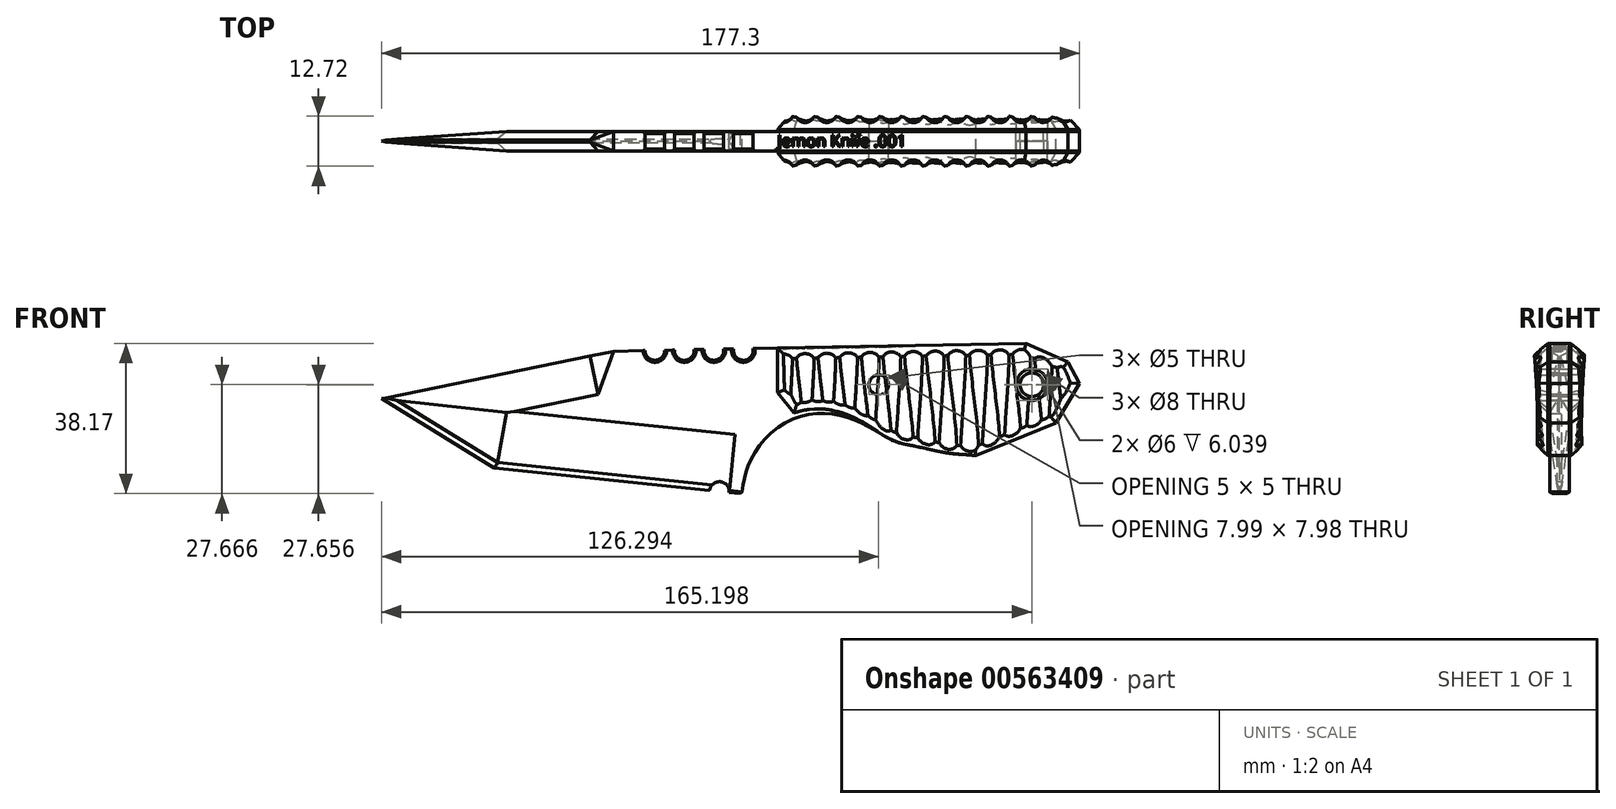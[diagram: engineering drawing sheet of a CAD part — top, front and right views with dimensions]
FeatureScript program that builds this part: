
annotation { "Feature Type Name" : "Feature", "Feature Type Description" : "" }
export const myFeature = defineFeature(function(context is Context, id is Id, definition is map)
    precondition{}
    {
        {
            var Q0;
            Q0=qCreatedBy(makeId("Front.planeOp"),FACE);
            var sketch = newSketch(context, id + "F0", { "sketchPlane" : qUnion([Q0])});
            skLineSegment(sketch, "E0", {"start": v(87.5, 0) * mm, "end": v(-87.5, 0) * mm, "construction": true});
            skLineSegment(sketch, "E1", {"start": v(-87.5, 0) * mm, "end": v(-28.6, 12.06) * mm});
            skLineSegment(sketch, "E2", {"start": v(-28.6, 12.06) * mm, "end": v(-20.58, 12.2) * mm});
            skLineSegment(sketch, "E3", {"start": v(76.15, 14.06) * mm, "end": v(86.87, 9.34) * mm});
            skLineSegment(sketch, "E4", {"start": v(86.87, 9.34) * mm, "end": v(89.8, 3.9) * mm});
            skLineSegment(sketch, "E5", {"start": v(89.8, 3.9) * mm, "end": v(83.87, -6.17) * mm});
            skLineSegment(sketch, "E6", {"start": v(83.87, -6.17) * mm, "end": v(63.5, -14.46) * mm});
            skLineSegment(sketch, "E7", {"start": v(-87.5, 0) * mm, "end": v(-58.95, -17.62) * mm});
            skLineSegment(sketch, "E8", {"start": v(-58.95, -17.62) * mm, "end": v(-4.16, -23.31) * mm});
            skFitSpline(sketch, "E9", {"points": [v(3.95, -24.15) * mm, v(5.88, -16.34) * mm, v(13.42, -7.16) * mm, v(24.63, -3.72) * mm, v(34.48, -6.24) * mm, v(42.3, -10.21) * mm, v(48.07, -12.01) * mm, v(55.88, -13.58) * mm, v(63.5, -14.46) * mm], "startDerivative": vector(14.8, 75.55) * mm, "endDerivative": vector(64.9, -6.2) * mm});
            skCircle(sketch, "E10", {"center": v(38.8, 3.56) * mm, "radius": 2.5 * mm});
            skCircle(sketch, "E11", {"center": v(77.7, 3.56) * mm, "radius": 4 * mm});
            skArc(sketch, "E12", {"start": v(-20.58, 12.2) * mm, "mid": v(-18.03, 9.76) * mm, "end": v(-15.58, 12.3) * mm});
            skArc(sketch, "E13.1.0.0", {"start": v(-13.08, 12.35) * mm, "mid": v(-10.53, 9.76) * mm, "end": v(-8.09, 12.45) * mm});
            skArc(sketch, "E13.2.0.0", {"start": v(-5.57, 12.5) * mm, "mid": v(-3.03, 9.76) * mm, "end": v(-0.6, 12.6) * mm});
            skArc(sketch, "E13.3.0.0", {"start": v(1.95, 12.64) * mm, "mid": v(4.47, 9.76) * mm, "end": v(6.87, 12.73) * mm});
            skLineSegment(sketch, "E13.direction1", {"start": v(-18.08, 12.26) * mm, "end": v(-10.58, 12.26) * mm, "construction": true});
            skLineSegment(sketch, "E14.trimOffspring", {"start": v(6.87, 12.73) * mm, "end": v(76.15, 14.06) * mm});
            skLineSegment(sketch, "E15.trimOffspring", {"start": v(-0.6, 12.6) * mm, "end": v(1.95, 12.64) * mm});
            skLineSegment(sketch, "E16.trimOffspring", {"start": v(-8.09, 12.45) * mm, "end": v(-5.57, 12.5) * mm});
            skLineSegment(sketch, "E17.trimOffspring", {"start": v(-15.58, 12.3) * mm, "end": v(-13.08, 12.35) * mm});
            skArc(sketch, "E18", {"start": v(0.82, -23.83) * mm, "mid": v(-1.41, -21.08) * mm, "end": v(-4.16, -23.31) * mm});
            skLineSegment(sketch, "E19.trimOffspring", {"start": v(0.82, -23.83) * mm, "end": v(3.95, -24.15) * mm});
            skSolve(sketch);
        }
        {
            var Q0;
            Q0 = qSketchRegion(id + "F0", true);
            extrude(context, id + "F1", {"entities" : qUnion([Q0]), "depth" : 5 * mm, "offsetDistance" : 25 * mm, "symmetric" : true});
        }
        {
            var Q0;
            Q0=makeQuery(id+"F1.opExtrude","SWEPT_FACE",FACE,{"disambiguationData":[OSD([sQuery(id+"F0.wireOp",EDGE,"E19.trimOffspring")])]});
            var Q1;
            Q1=makeQuery(id+"F1.opExtrude","SWEPT_EDGE",EDGE,{"disambiguationData":[OSD([sQuery(id+"F0.wireOp",EDGE,"E18"),sQuery(id+"F0.wireOp",EDGE,"E19.trimOffspring")])]});
            cPlane(context, id + "F2", {"entities" : qUnion([Q0, Q1]), "cplaneType" : CPlaneType.LINE_ANGLE, "offset" : 25 * mm, "angle" : 90 * degree, "width" : 150 * mm, "height" : 150 * mm});
        }
        {
            var Q0;
            Q0=qCreatedBy(id+"F2.planeOp",FACE);
            var sketch = newSketch(context, id + "F3", { "sketchPlane" : qUnion([Q0])});
            skLineSegment(sketch, "E20", {"start": v(0, -23.94) * mm, "end": v(0, -10.63) * mm, "construction": true});
            skLineSegment(sketch, "E21", {"start": v(-2.53, -8.62) * mm, "end": v(-2.53, -24.28) * mm});
            skLineSegment(sketch, "E22", {"start": v(-2.53, -24.28) * mm, "end": v(0, -24.28) * mm});
            skLineSegment(sketch, "E23", {"start": v(0, -23.94) * mm, "end": v(-0.25, -23.94) * mm});
            skLineSegment(sketch, "E24", {"start": v(-0.25, -23.94) * mm, "end": v(-2.53, -8.62) * mm});
            skLineSegment(sketch, "E25.MirrorCS", {"start": v(0.25, -23.94) * mm, "end": v(2.53, -8.62) * mm});
            skLineSegment(sketch, "E26.MirrorCS", {"start": v(0, -23.94) * mm, "end": v(0.25, -23.94) * mm});
            skLineSegment(sketch, "E27.MirrorCS", {"start": v(2.53, -24.28) * mm, "end": v(0, -24.28) * mm});
            skLineSegment(sketch, "E28.MirrorCS", {"start": v(2.53, -8.62) * mm, "end": v(2.53, -24.28) * mm});
            skSolve(sketch);
        }
        {
            var Q0;
            Q0 = qSketchRegion(id + "F3", true);
            extrude(context, id + "F4", {"entities" : qUnion([Q0]), "operationType" : NewBodyOperationType.REMOVE, "endBound" : BoundingType.THROUGH_ALL, "oppositeDirection" : true, "depth" : 25 * mm, "offsetDistance" : 25 * mm});
        }
        {
            var Q0;
            Q0=makeQuery(id+"F1.opExtrude","SWEPT_FACE",FACE,{"disambiguationData":[OSD([sQuery(id+"F0.wireOp",EDGE,"E7")])]});
            var Q1;
            Q1=makeQuery(id+"F1.opExtrude","SWEPT_EDGE",EDGE,{"disambiguationData":[OSD([sQuery(id+"F0.wireOp",EDGE,"E1"),sQuery(id+"F0.wireOp",EDGE,"E7")])]});
            cPlane(context, id + "F5", {"entities" : qUnion([Q0, Q1]), "cplaneType" : CPlaneType.LINE_ANGLE, "offset" : 25 * mm, "angle" : 90 * degree, "width" : 150 * mm, "height" : 150 * mm});
        }
        {
            var Q0;
            Q0=makeQuery(id+"F1.opExtrude","SWEPT_FACE",FACE,{"disambiguationData":[OSD([sQuery(id+"F0.wireOp",EDGE,"E1")])]});
            var Q1;
            Q1=makeQuery(id+"F1.opExtrude","SWEPT_EDGE",EDGE,{"disambiguationData":[OSD([sQuery(id+"F0.wireOp",EDGE,"E1"),sQuery(id+"F0.wireOp",EDGE,"E7")])]});
            cPlane(context, id + "F6", {"entities" : qUnion([Q0, Q1]), "cplaneType" : CPlaneType.LINE_ANGLE, "offset" : 25 * mm, "angle" : 90 * degree, "width" : 150 * mm, "height" : 150 * mm});
        }
        {
            var Q0;
            Q0=qCreatedBy(id+"F5.planeOp",FACE);
            var sketch = newSketch(context, id + "F7", { "sketchPlane" : qUnion([Q0])});
            skLineSegment(sketch, "E29", {"start": v(0, -45.96) * mm, "end": v(0, -23.67) * mm, "construction": true});
            skLineSegment(sketch, "E30", {"start": v(0, -45.96) * mm, "end": v(0.25, -45.96) * mm});
            skLineSegment(sketch, "E31", {"start": v(0.25, -45.96) * mm, "end": v(2.5, -31.86) * mm});
            skLineSegment(sketch, "E32", {"start": v(2.5, -31.86) * mm, "end": v(2.5, -46.86) * mm});
            skLineSegment(sketch, "E33", {"start": v(2.5, -46.86) * mm, "end": v(0, -46.86) * mm});
            skLineSegment(sketch, "E34.MirrorCS", {"start": v(-0.25, -45.96) * mm, "end": v(-2.5, -31.86) * mm});
            skLineSegment(sketch, "E35.MirrorCS", {"start": v(-2.5, -31.86) * mm, "end": v(-2.5, -46.86) * mm});
            skLineSegment(sketch, "E36.MirrorCS", {"start": v(-2.5, -46.86) * mm, "end": v(0, -46.86) * mm});
            skLineSegment(sketch, "E37.MirrorCS", {"start": v(0, -45.96) * mm, "end": v(-0.25, -45.96) * mm});
            skSolve(sketch);
        }
        {
            var Q0;
            Q0 = qSketchRegion(id + "F7", true);
            extrude(context, id + "F8", {"entities" : qUnion([Q0]), "operationType" : NewBodyOperationType.REMOVE, "endBound" : BoundingType.THROUGH_ALL, "depth" : 25 * mm, "offsetDistance" : 25 * mm});
        }
        {
            var Q0;
            Q0=qCreatedBy(id+"F6.planeOp",FACE);
            var sketch = newSketch(context, id + "F9", { "sketchPlane" : qUnion([Q0])});
            skFitSpline(sketch, "E38.0", {"points": [v(0.25, 17.54) * mm, v(0.08, 17.54) * mm, v(-0.08, 17.54) * mm, v(-0.25, 17.54) * mm], "construction": true});
            skFitSpline(sketch, "E39.0", {"points": [v(2.5, 17.54) * mm, v(2.5, 14.4) * mm, v(2.5, 11.26) * mm, v(2.5, 8.12) * mm], "construction": true});
            skLineSegment(sketch, "E40", {"start": v(0, 17.54) * mm, "end": v(0, 7.44) * mm, "construction": true});
            skLineSegment(sketch, "E41", {"start": v(2.5, 17.54) * mm, "end": v(2.5, 7.54) * mm});
            skLineSegment(sketch, "E42", {"start": v(2.5, 7.54) * mm, "end": v(0.25, 17.54) * mm});
            skLineSegment(sketch, "E43", {"start": v(2.5, 17.54) * mm, "end": v(2.5, 18.15) * mm});
            skLineSegment(sketch, "E44", {"start": v(2.5, 18.15) * mm, "end": v(0, 18.15) * mm});
            skLineSegment(sketch, "E45.MirrorCS", {"start": v(-2.5, 18.15) * mm, "end": v(0, 18.15) * mm});
            skLineSegment(sketch, "E46.MirrorCS", {"start": v(-2.5, 7.54) * mm, "end": v(-0.25, 17.54) * mm});
            skLineSegment(sketch, "E47.MirrorCS", {"start": v(-2.5, 17.54) * mm, "end": v(-2.5, 18.15) * mm});
            skFitSpline(sketch, "E48.MirrorCS", {"points": [v(-2.5, 17.54) * mm, v(-2.5, 14.4) * mm, v(-2.5, 11.26) * mm, v(-2.5, 8.12) * mm], "construction": true});
            skLineSegment(sketch, "E49.MirrorCS", {"start": v(-2.5, 17.54) * mm, "end": v(-2.5, 7.54) * mm});
            skLineSegment(sketch, "E50", {"start": v(-0.25, 17.54) * mm, "end": v(0.25, 17.54) * mm});
            skSolve(sketch);
        }
        {
            var Q0;
            Q0 = qSketchRegion(id + "F9", true);
            var Q1;
            Q1=makeQuery(id+"F1.opExtrude","CAP_VERTEX",VERTEX,{"disambiguationData":[OSD([sQuery(id+"F0.wireOp",EDGE,"E1"),sQuery(id+"F0.wireOp",EDGE,"E2")])],"isStart":false});
            extrude(context, id + "F10", {"entities" : qUnion([Q0]), "operationType" : NewBodyOperationType.REMOVE, "endBound" : BoundingType.UP_TO_VERTEX, "oppositeDirection" : true, "depth" : 57.81 * mm, "endBoundEntityVertex" : qUnion([Q1]), "offsetDistance" : 25 * mm});
        }
        {
            var Q0;
            Q0=makeQuery(id+"F10.boolean.opBoolean","COPY",EDGE,{"derivedFrom":makeQuery(id+"F10.opExtrude","CAP_EDGE",EDGE,{"disambiguationData":[OSD([sQuery(id+"F9.wireOp",EDGE,"E42")])],"isStart":false})});
            chamfer(context, id + "F11", {"entities" : qUnion([Q0]), "chamferType" : ChamferType.OFFSET_ANGLE, "width" : 2.19 * mm, "oppositeDirection" : true, "angle" : 70 * degree, "tangentPropagation" : true});
        }
        {
            var Q0;
            Q0=makeQuery(id+"F10.boolean.opBoolean","COPY",EDGE,{"derivedFrom":makeQuery(id+"F10.opExtrude","CAP_EDGE",EDGE,{"disambiguationData":[OSD([sQuery(id+"F9.wireOp",EDGE,"E46.MirrorCS")])],"isStart":false})});
            chamfer(context, id + "F12", {"entities" : qUnion([Q0]), "chamferType" : ChamferType.OFFSET_ANGLE, "width" : 2.19 * mm, "oppositeDirection" : false, "angle" : 70 * degree, "tangentPropagation" : true});
        }
        {
            var Q0;
            Q0=makeQuery(id+"F1.opExtrude","CAP_FACE",FACE,{"disambiguationData":[OSD([sQuery(id+"F0.wireOp",EDGE,"E1"),sQuery(id+"F0.wireOp",EDGE,"E2"),sQuery(id+"F0.wireOp",EDGE,"E3"),sQuery(id+"F0.wireOp",EDGE,"E4"),sQuery(id+"F0.wireOp",EDGE,"E5"),sQuery(id+"F0.wireOp",EDGE,"E6"),sQuery(id+"F0.wireOp",EDGE,"E7"),sQuery(id+"F0.wireOp",EDGE,"E8"),sQuery(id+"F0.wireOp",EDGE,"E9"),sQuery(id+"F0.wireOp",EDGE,"E10"),sQuery(id+"F0.wireOp",EDGE,"E11"),sQuery(id+"F0.wireOp",EDGE,"E12"),sQuery(id+"F0.wireOp",EDGE,"E13.1.0.0"),sQuery(id+"F0.wireOp",EDGE,"E13.2.0.0"),sQuery(id+"F0.wireOp",EDGE,"E13.3.0.0"),sQuery(id+"F0.wireOp",EDGE,"E14.trimOffspring"),sQuery(id+"F0.wireOp",EDGE,"E15.trimOffspring"),sQuery(id+"F0.wireOp",EDGE,"E16.trimOffspring"),sQuery(id+"F0.wireOp",EDGE,"E17.trimOffspring"),sQuery(id+"F0.wireOp",EDGE,"E18"),sQuery(id+"F0.wireOp",EDGE,"E19.trimOffspring")])],"isStart":false});
            var sketch = newSketch(context, id + "F13", { "sketchPlane" : qUnion([Q0])});
            skLineSegment(sketch, "E51.0", {"start": v(13.04, 12.85) * mm, "end": v(76.15, 14.06) * mm});
            skLineSegment(sketch, "E52.0", {"start": v(76.15, 14.06) * mm, "end": v(86.87, 9.34) * mm});
            skLineSegment(sketch, "E53.0", {"start": v(86.87, 9.34) * mm, "end": v(89.8, 3.9) * mm});
            skLineSegment(sketch, "E54.0", {"start": v(89.8, 3.9) * mm, "end": v(83.87, -6.17) * mm});
            skLineSegment(sketch, "E55.0", {"start": v(83.87, -6.17) * mm, "end": v(63.5, -14.46) * mm});
            skFitSpline(sketch, "E56.0", {"points": [v(3.95, -24.15) * mm, v(4.54, -21.17) * mm, v(5, -16.2) * mm, v(12.74, -5.92) * mm, v(24.62, -2.63) * mm, v(34.48, -5.81) * mm, v(42.13, -10.52) * mm, v(48.02, -12.06) * mm, v(55.94, -13.74) * mm, v(61, -14.22) * mm, v(63.5, -14.46) * mm]});
            skLineSegment(sketch, "E57", {"start": v(13.04, 12.85) * mm, "end": v(13.04, 1.61) * mm});
            skLineSegment(sketch, "E58", {"start": v(13.04, 1.61) * mm, "end": v(18.26, -4.73) * mm});
            skCircle(sketch, "E59.0", {"center": v(38.8, 3.56) * mm, "radius": 2.5 * mm});
            skCircle(sketch, "E60.0", {"center": v(77.7, 3.56) * mm, "radius": 4 * mm});
            skSolve(sketch);
        }
        {
            var Q0;
            Q0 = qSketchRegion(id + "F13", true);
            extrude(context, id + "F14", {"entities" : qUnion([Q0]), "depth" : 4 * mm, "offsetDistance" : 25 * mm});
        }
        {
            var Q0;
            Q0=makeQuery(id+"F14.opExtrude","CAP_EDGE",EDGE,{"disambiguationData":[OSD([sQuery(id+"F13.wireOp",EDGE,"E57")])],"isStart":false});
            var Q1;
            Q1=makeQuery(id+"F14.opExtrude","CAP_EDGE",EDGE,{"disambiguationData":[OSD([sQuery(id+"F13.wireOp",EDGE,"E51.0")])],"isStart":false});
            var Q2;
            Q2=makeQuery(id+"F14.opExtrude","CAP_EDGE",EDGE,{"disambiguationData":[OSD([sQuery(id+"F13.wireOp",EDGE,"E52.0")])],"isStart":false});
            var Q3;
            Q3=makeQuery(id+"F14.opExtrude","CAP_EDGE",EDGE,{"disambiguationData":[OSD([sQuery(id+"F13.wireOp",EDGE,"E53.0")])],"isStart":false});
            var Q4;
            Q4=makeQuery(id+"F14.opExtrude","CAP_EDGE",EDGE,{"disambiguationData":[OSD([sQuery(id+"F13.wireOp",EDGE,"E54.0")])],"isStart":false});
            var Q5;
            Q5=makeQuery(id+"F14.opExtrude","CAP_EDGE",EDGE,{"disambiguationData":[OSD([sQuery(id+"F13.wireOp",EDGE,"E55.0")])],"isStart":false});
            var Q6;
            Q6=makeQuery(id+"F14.opExtrude","CAP_EDGE",EDGE,{"disambiguationData":[OSD([sQuery(id+"F13.wireOp",EDGE,"E56.0")])],"isStart":false});
            var Q7;
            Q7=makeQuery(id+"F14.opExtrude","CAP_EDGE",EDGE,{"disambiguationData":[OSD([sQuery(id+"F13.wireOp",EDGE,"E58")])],"isStart":false});
            chamfer(context, id + "F15", {"entities" : qUnion([Q0, Q1, Q2, Q3, Q4, Q5, Q6, Q7]), "chamferType" : ChamferType.OFFSET_ANGLE, "width" : 3 * mm, "oppositeDirection" : false, "angle" : 50 * degree, "tangentPropagation" : true});
        }
        {
            var Q0;
            Q0=qCreatedBy(id+"F2.planeOp",FACE);
            var sketch = newSketch(context, id + "F16", { "sketchPlane" : qUnion([Q0])});
            skLineSegment(sketch, "E61.0", {"start": v(-0.3, -23.62) * mm, "end": v(0.3, -23.62) * mm, "construction": true});
            skLineSegment(sketch, "E62", {"start": v(0, -23.62) * mm, "end": v(0, -22.12) * mm, "construction": true});
            skPoint(sketch, "E62.startSnap0", {"position": v(0, -23.62) * mm});
            skLineSegment(sketch, "E63", {"start": v(-0.53, -22.12) * mm, "end": v(-0.5, -23.75) * mm});
            skLineSegment(sketch, "E64", {"start": v(-0.5, -23.75) * mm, "end": v(0, -23.74) * mm});
            skLineSegment(sketch, "E65", {"start": v(-0.53, -22.12) * mm, "end": v(0, -23.62) * mm});
            skLineSegment(sketch, "E66.MirrorCS", {"start": v(0.53, -22.12) * mm, "end": v(0, -23.62) * mm});
            skLineSegment(sketch, "E67.MirrorCS", {"start": v(0.53, -22.12) * mm, "end": v(0.5, -23.75) * mm});
            skLineSegment(sketch, "E68.MirrorCS", {"start": v(0.5, -23.75) * mm, "end": v(0, -23.74) * mm});
            skSolve(sketch);
        }
        {
            var Q0;
            Q0 = qSketchRegion(id + "F16", true);
            extrude(context, id + "F17", {"entities" : qUnion([Q0]), "operationType" : NewBodyOperationType.REMOVE, "endBound" : BoundingType.THROUGH_ALL, "oppositeDirection" : true, "depth" : 25 * mm, "offsetDistance" : 25 * mm});
        }
        {
            var Q0;
            Q0=qCreatedBy(id+"F5.planeOp",FACE);
            var sketch = newSketch(context, id + "F18", { "sketchPlane" : qUnion([Q0])});
            skFitSpline(sketch, "E69.0", {"points": [v(-0.25, -45.96) * mm, v(-0.08, -45.96) * mm, v(0.08, -45.96) * mm, v(0.25, -45.96) * mm], "construction": true});
            skLineSegment(sketch, "E70", {"start": v(0, -45.96) * mm, "end": v(0, -44.2) * mm, "construction": true});
            skLineSegment(sketch, "E71", {"start": v(0.54, -44.2) * mm, "end": v(0.54, -46.08) * mm});
            skLineSegment(sketch, "E72", {"start": v(0.54, -46.08) * mm, "end": v(0, -46.08) * mm});
            skPoint(sketch, "E73.orphan", {"position": v(2.45, -32.2) * mm});
            skPoint(sketch, "E74.0.start.orphan", {"position": v(0.25, -45.96) * mm});
            skLineSegment(sketch, "E75", {"start": v(0, -45.96) * mm, "end": v(0.54, -44.2) * mm});
            skLineSegment(sketch, "E76.MirrorCS", {"start": v(0, -45.96) * mm, "end": v(-0.54, -44.2) * mm});
            skLineSegment(sketch, "E77.MirrorCS", {"start": v(-0.54, -44.2) * mm, "end": v(-0.54, -46.08) * mm});
            skLineSegment(sketch, "E78.MirrorCS", {"start": v(-0.54, -46.08) * mm, "end": v(0, -46.08) * mm});
            skSolve(sketch);
        }
        {
            var Q0;
            Q0 = qSketchRegion(id + "F18", true);
            extrude(context, id + "F19", {"entities" : qUnion([Q0]), "operationType" : NewBodyOperationType.REMOVE, "endBound" : BoundingType.THROUGH_ALL, "depth" : 25 * mm, "offsetDistance" : 25 * mm});
        }
        {
            var Q0;
            Q0=makeQuery(id+"F14.opExtrude","CAP_FACE",FACE,{"disambiguationData":[OSD([sQuery(id+"F13.wireOp",EDGE,"E51.0"),sQuery(id+"F13.wireOp",EDGE,"E52.0"),sQuery(id+"F13.wireOp",EDGE,"E53.0"),sQuery(id+"F13.wireOp",EDGE,"E54.0"),sQuery(id+"F13.wireOp",EDGE,"E55.0"),sQuery(id+"F13.wireOp",EDGE,"E56.0"),sQuery(id+"F13.wireOp",EDGE,"E57"),sQuery(id+"F13.wireOp",EDGE,"E58"),sQuery(id+"F13.wireOp",EDGE,"E59.0"),sQuery(id+"F13.wireOp",EDGE,"E60.0")])],"isStart":false});
            var sketch = newSketch(context, id + "F20", { "sketchPlane" : qUnion([Q0])});
            skCircle(sketch, "E79.0", {"center": v(38.8, 3.56) * mm, "radius": 2.5 * mm});
            skSolve(sketch);
        }
        {
            var Q0;
            Q0 = qSketchRegion(id + "F20", true);
            extrude(context, id + "F21", {"entities" : qUnion([Q0]), "oppositeDirection" : true, "depth" : 6.5 * mm, "offsetDistance" : 25 * mm});
        }
        {
            var Q0;
            Q0=makeQuery(id+"F14.opExtrude","CAP_FACE",FACE,{"disambiguationData":[OSD([sQuery(id+"F13.wireOp",EDGE,"E51.0"),sQuery(id+"F13.wireOp",EDGE,"E52.0"),sQuery(id+"F13.wireOp",EDGE,"E53.0"),sQuery(id+"F13.wireOp",EDGE,"E54.0"),sQuery(id+"F13.wireOp",EDGE,"E55.0"),sQuery(id+"F13.wireOp",EDGE,"E56.0"),sQuery(id+"F13.wireOp",EDGE,"E57"),sQuery(id+"F13.wireOp",EDGE,"E58"),sQuery(id+"F13.wireOp",EDGE,"E59.0"),sQuery(id+"F13.wireOp",EDGE,"E60.0")])],"isStart":false});
            var sketch = newSketch(context, id + "F22", { "sketchPlane" : qUnion([Q0])});
            skCircle(sketch, "E80.0", {"center": v(77.7, 3.56) * mm, "radius": 4 * mm});
            skCircle(sketch, "E81", {"center": v(77.7, 3.56) * mm, "radius": 3 * mm});
            skSolve(sketch);
        }
        {
            var Q0;
            Q0 = qSketchRegion(id + "F22", true);
            extrude(context, id + "F23", {"entities" : qUnion([Q0]), "oppositeDirection" : true, "depth" : 6.5 * mm, "offsetDistance" : 25 * mm});
        }
        {
            var Q0;
            Q0=makeQuery(id+"F1.opExtrude","SWEPT_FACE",FACE,{"disambiguationData":[OSD([sQuery(id+"F0.wireOp",EDGE,"E14.trimOffspring")])]});
            var Q1;
            Q1=makeQuery(id+"F14.opExtrude","CAP_EDGE",EDGE,{"disambiguationData":[OSD([sQuery(id+"F13.wireOp",EDGE,"E51.0")])],"isStart":true});
            cPlane(context, id + "F24", {"entities" : qUnion([Q0, Q1]), "cplaneType" : CPlaneType.LINE_ANGLE, "offset" : 25 * mm, "angle" : 178 * degree, "width" : 150 * mm, "height" : 150 * mm});
        }
        {
            var Q0;
            Q0=qCreatedBy(id+"F24.planeOp",FACE);
            var sketch = newSketch(context, id + "F25", { "sketchPlane" : qUnion([Q0])});
            skLineSegment(sketch, "E82", {"start": v(14.78, -7.64) * mm, "end": v(83.87, -7.64) * mm, "construction": true});
            skCircle(sketch, "E83", {"center": v(14.78, -7.64) * mm, "radius": 2.5 * mm});
            skCircle(sketch, "E84.1.0.0", {"center": v(20.28, -7.64) * mm, "radius": 2.5 * mm});
            skCircle(sketch, "E84.2.0.0", {"center": v(25.78, -7.64) * mm, "radius": 2.5 * mm});
            skCircle(sketch, "E84.3.0.0", {"center": v(31.28, -7.64) * mm, "radius": 2.5 * mm});
            skCircle(sketch, "E84.4.0.0", {"center": v(36.78, -7.64) * mm, "radius": 2.5 * mm});
            skCircle(sketch, "E84.5.0.0", {"center": v(42.28, -7.64) * mm, "radius": 2.5 * mm});
            skCircle(sketch, "E84.6.0.0", {"center": v(47.78, -7.64) * mm, "radius": 2.5 * mm});
            skCircle(sketch, "E84.7.0.0", {"center": v(53.28, -7.64) * mm, "radius": 2.5 * mm});
            skCircle(sketch, "E84.8.0.0", {"center": v(58.78, -7.64) * mm, "radius": 2.5 * mm});
            skCircle(sketch, "E84.9.0.0", {"center": v(64.28, -7.64) * mm, "radius": 2.5 * mm});
            skCircle(sketch, "E84.10.0.0", {"center": v(69.78, -7.64) * mm, "radius": 2.5 * mm});
            skCircle(sketch, "E84.11.0.0", {"center": v(75.28, -7.64) * mm, "radius": 2.5 * mm});
            skLineSegment(sketch, "E84.direction1", {"start": v(14.78, -7.64) * mm, "end": v(20.28, -7.64) * mm, "construction": true});
            skCircle(sketch, "E85.0.12.0", {"center": v(80.78, -7.64) * mm, "radius": 2.5 * mm});
            skCircle(sketch, "E85.0.13.0", {"center": v(86.28, -7.64) * mm, "radius": 2.5 * mm});
            skSolve(sketch);
        }
        {
            var Q0;
            Q0 = qSketchRegion(id + "F25", true);
            var Q1;
            Q1=sQuery(id+"F25.wireOp",EDGE,"E82");
            extrude(context, id + "F26", {"entities" : qUnion([Q0]), "operationType" : NewBodyOperationType.REMOVE, "surfaceEntities" : qUnion([Q1]), "endBound" : BoundingType.THROUGH_ALL, "oppositeDirection" : true, "depth" : 25 * mm, "offsetDistance" : 25 * mm});
        }
        {
            var Q0;
            Q0=qCreatedBy(makeId("Top.planeOp"),FACE);
            cPlane(context, id + "F27", {"entities" : qUnion([Q0]), "cplaneType" : CPlaneType.OFFSET, "offset" : 15 * mm, "oppositeDirection" : true, "width" : 150 * mm, "height" : 150 * mm});
        }
        {
            var Q0;
            Q0=qCreatedBy(id+"F27.planeOp",FACE);
            var sketch = newSketch(context, id + "F28", { "sketchPlane" : qUnion([Q0])});
            skLineSegment(sketch, "E86.0", {"start": v(89.8, -2.5) * mm, "end": v(89.8, 2.5) * mm, "construction": true});
            skLineSegment(sketch, "E87", {"start": v(118.57, 0) * mm, "end": v(61.03, 0) * mm, "construction": true});
            skPoint(sketch, "E87.startSnap0", {"position": v(89.8, 0) * mm});
            skPoint(sketch, "E87.endSnap0", {"position": v(89.8, 0) * mm});
            skSolve(sketch);
        }
        {
            var Q0;
            Q0=qCreatedBy(id+"F27.planeOp",FACE);
            var Q1;
            Q1=sQuery(id+"F28.wireOp",EDGE,"E87");
            cPlane(context, id + "F29", {"entities" : qUnion([Q0, Q1]), "cplaneType" : CPlaneType.LINE_ANGLE, "offset" : 25 * mm, "angle" : 175 * degree, "width" : 150 * mm, "height" : 150 * mm});
        }
        {
            var Q0;
            Q0=qCreatedBy(id+"F29.planeOp",FACE);
            var sketch = newSketch(context, id + "F30", { "sketchPlane" : qUnion([Q0])});
            skCircle(sketch, "E88", {"center": v(17.9, -7.67) * mm, "radius": 2.5 * mm});
            skCircle(sketch, "E89.1.0.0", {"center": v(23.4, -7.67) * mm, "radius": 2.5 * mm});
            skCircle(sketch, "E89.2.0.0", {"center": v(28.9, -7.67) * mm, "radius": 2.5 * mm});
            skCircle(sketch, "E89.3.0.0", {"center": v(34.4, -7.67) * mm, "radius": 2.5 * mm});
            skCircle(sketch, "E89.4.0.0", {"center": v(39.9, -7.67) * mm, "radius": 2.5 * mm});
            skCircle(sketch, "E89.5.0.0", {"center": v(45.4, -7.67) * mm, "radius": 2.5 * mm});
            skCircle(sketch, "E89.6.0.0", {"center": v(50.9, -7.67) * mm, "radius": 2.5 * mm});
            skCircle(sketch, "E89.7.0.0", {"center": v(56.4, -7.67) * mm, "radius": 2.5 * mm});
            skCircle(sketch, "E89.8.0.0", {"center": v(61.9, -7.67) * mm, "radius": 2.5 * mm});
            skCircle(sketch, "E89.9.0.0", {"center": v(67.4, -7.67) * mm, "radius": 2.5 * mm});
            skCircle(sketch, "E89.10.0.0", {"center": v(72.9, -7.67) * mm, "radius": 2.5 * mm});
            skCircle(sketch, "E89.11.0.0", {"center": v(78.4, -7.67) * mm, "radius": 2.5 * mm});
            skCircle(sketch, "E89.12.0.0", {"center": v(83.9, -7.67) * mm, "radius": 2.5 * mm});
            skLineSegment(sketch, "E89.direction1", {"start": v(17.9, -7.67) * mm, "end": v(23.4, -7.67) * mm, "construction": true});
            skSolve(sketch);
        }
        {
            var Q0;
            Q0 = qSketchRegion(id + "F30", true);
            extrude(context, id + "F31", {"entities" : qUnion([Q0]), "operationType" : NewBodyOperationType.REMOVE, "endBound" : BoundingType.THROUGH_ALL, "depth" : 25 * mm, "offsetDistance" : 25 * mm});
        }
        {
            var Q0;
            Q0=makeQuery(id+"F14.opExtrude","SWEPT_BODY",BODY,{"disambiguationData":[OSD([sQuery(id+"F13.wireOp",EDGE,"E51.0"),sQuery(id+"F13.wireOp",EDGE,"E52.0"),sQuery(id+"F13.wireOp",EDGE,"E53.0"),sQuery(id+"F13.wireOp",EDGE,"E54.0"),sQuery(id+"F13.wireOp",EDGE,"E55.0"),sQuery(id+"F13.wireOp",EDGE,"E56.0"),sQuery(id+"F13.wireOp",EDGE,"E57"),sQuery(id+"F13.wireOp",EDGE,"E58"),sQuery(id+"F13.wireOp",EDGE,"E59.0"),sQuery(id+"F13.wireOp",EDGE,"E60.0")])]});
            var Q1;
            Q1=makeQuery(id+"F21.opExtrude","SWEPT_BODY",BODY,{"disambiguationData":[OSD([sQuery(id+"F20.wireOp",EDGE,"E79.0")])]});
            var Q2;
            Q2=makeQuery(id+"F23.opExtrude","SWEPT_BODY",BODY,{"disambiguationData":[OSD([sQuery(id+"F22.wireOp",EDGE,"E80.0"),sQuery(id+"F22.wireOp",EDGE,"E81")])]});
            var Q3;
            Q3=qCreatedBy(makeId("Front.planeOp"),FACE);
            mirror(context, id + "F32", {"entities" : qUnion([Q0, Q1, Q2]), "mirrorPlane" : qUnion([Q3])});
        }
        {
            var Q0;
            Q0=makeQuery(id+"F1.opExtrude","CAP_EDGE",EDGE,{"disambiguationData":[OSD([sQuery(id+"F0.wireOp",EDGE,"E19.trimOffspring")])],"isStart":false});
            var Q1;
            Q1=makeQuery(id+"F1.opExtrude","CAP_EDGE",EDGE,{"disambiguationData":[OSD([sQuery(id+"F0.wireOp",EDGE,"E19.trimOffspring")])],"isStart":true});
            var Q2;
            Q2=makeQuery(id+"F1.opExtrude","SWEPT_EDGE",EDGE,{"disambiguationData":[OSD([sQuery(id+"F0.wireOp",EDGE,"E9"),sQuery(id+"F0.wireOp",EDGE,"E19.trimOffspring")])]});
            var Q3;
            Q3=makeQuery(id+"F1.opExtrude","CAP_EDGE",EDGE,{"disambiguationData":[OSD([sQuery(id+"F0.wireOp",EDGE,"E13.3.0.0")])],"isStart":false});
            var Q4;
            Q4=makeQuery(id+"F1.opExtrude","CAP_EDGE",EDGE,{"disambiguationData":[OSD([sQuery(id+"F0.wireOp",EDGE,"E13.2.0.0")])],"isStart":false});
            var Q5;
            Q5=makeQuery(id+"F1.opExtrude","CAP_EDGE",EDGE,{"disambiguationData":[OSD([sQuery(id+"F0.wireOp",EDGE,"E13.1.0.0")])],"isStart":false});
            var Q6;
            Q6=makeQuery(id+"F1.opExtrude","CAP_EDGE",EDGE,{"disambiguationData":[OSD([sQuery(id+"F0.wireOp",EDGE,"E12")])],"isStart":false});
            var Q7;
            Q7=makeQuery(id+"F1.opExtrude","CAP_EDGE",EDGE,{"disambiguationData":[OSD([sQuery(id+"F0.wireOp",EDGE,"E12")])],"isStart":true});
            var Q8;
            Q8=makeQuery(id+"F1.opExtrude","CAP_EDGE",EDGE,{"disambiguationData":[OSD([sQuery(id+"F0.wireOp",EDGE,"E13.1.0.0")])],"isStart":true});
            var Q9;
            Q9=makeQuery(id+"F1.opExtrude","CAP_EDGE",EDGE,{"disambiguationData":[OSD([sQuery(id+"F0.wireOp",EDGE,"E13.2.0.0")])],"isStart":true});
            var Q10;
            Q10=makeQuery(id+"F1.opExtrude","CAP_EDGE",EDGE,{"disambiguationData":[OSD([sQuery(id+"F0.wireOp",EDGE,"E13.3.0.0")])],"isStart":true});
            chamfer(context, id + "F33", {"entities" : qUnion([Q0, Q1, Q2, Q3, Q4, Q5, Q6, Q7, Q8, Q9, Q10]), "width" : .5 * mm, "tangentPropagation" : true});
        }
        {
            var Q0;
            Q0=makeQuery(id+"F1.opExtrude","SWEPT_FACE",FACE,{"disambiguationData":[OSD([sQuery(id+"F0.wireOp",EDGE,"E14.trimOffspring")])]});
            var sketch = newSketch(context, id + "F34", { "sketchPlane" : qUnion([Q0])});
            skText(sketch, "E90", { "text": "Jemon Knife .001", "fontName": "OpenSans-Regular.ttf"});
            const initialGuessF34  = {"E90": [0.01327, -0.0014, 1, 0, 0.003]};
            skSetInitialGuess(sketch, initialGuessF34);
            skSolve(sketch);
        }
        {
            var Q0;
            Q0 = qSketchRegion(id + "F34", true);
            extrude(context, id + "F35", {"entities" : qUnion([Q0]), "operationType" : NewBodyOperationType.REMOVE, "oppositeDirection" : true, "depth" : .2 * mm, "offsetDistance" : 25 * mm});
        }
    });
